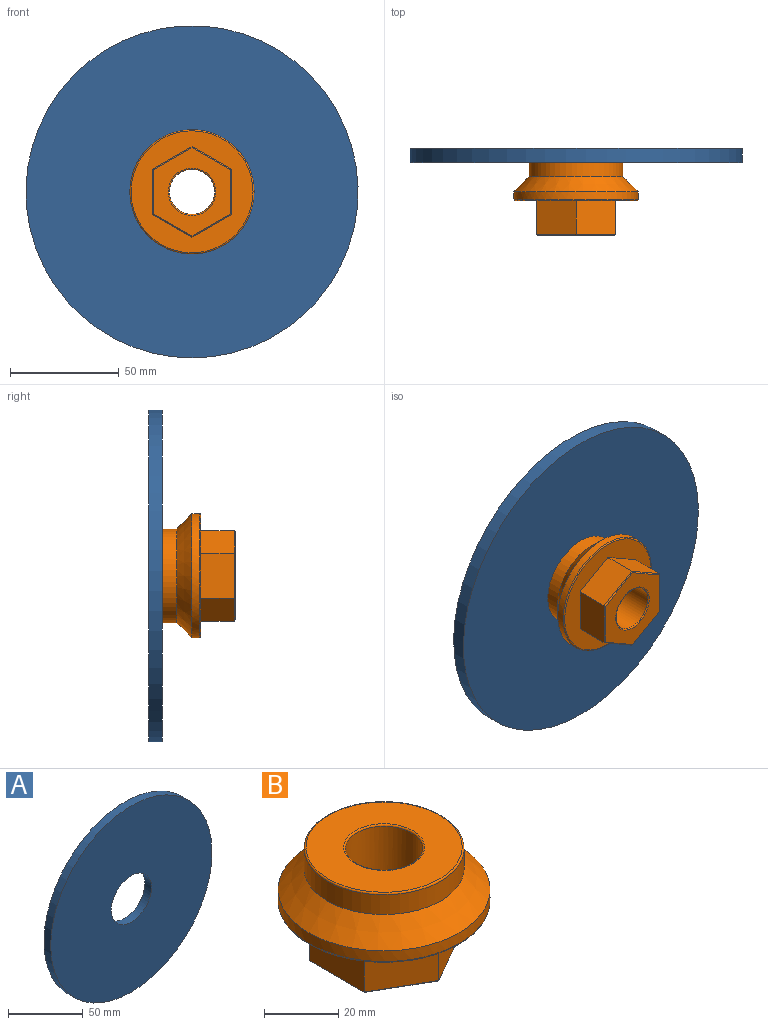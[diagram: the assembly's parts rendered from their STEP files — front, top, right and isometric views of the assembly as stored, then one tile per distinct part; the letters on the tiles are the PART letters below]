
ASSEMBLY  parts=2 mates=1
PART A: 4 faces, bbox 152.4x6.4x152.4 mm
  f0: cylinder r=19.05mm len=38.1mm, axis (0,1,0), area 760.1mm2, adj f2,f3
  f1: cylinder r=76.2mm len=152.4mm, axis (0,1,0), area 3040.2mm2, adj f2,f3
  f2: plane 152.4x152.4mm, normal (0,-1,0), area 17101.4mm2, adj f0,f1
  f3: plane 152.4x152.4mm, normal (0,1,0), area 17101.4mm2, adj f0,f1
PART B: 23 faces, bbox 61.7x61.7x34 mm
  f0: plane 18x10.68mm, normal (-0.35,-0.61,-0.71), area 14.5mm2, adj f4,f5,f9,f21
  f1: plane 18x10.68mm, normal (-0.35,0.61,-0.71), area 14.5mm2, adj f2,f5,f8,f9
  f2: plane 18x10.68mm, normal (0.35,0.61,-0.71), area 14.5mm2, adj f1,f3,f7,f9
  f3: plane 20.78x0.5mm, normal (0.71,0,-0.71), area 14.5mm2, adj f2,f4,f6,f9
  f4: plane 18x10.68mm, normal (0.35,-0.61,-0.71), area 14.5mm2, adj f0,f3,f9,f20
  f5: plane 20.78x0.5mm, normal (-0.71,0,-0.71), area 14.5mm2, adj f0,f1,f9,f22
  f6: plane 20.78x15.5mm, normal (1,0,0), area 322.2mm2, adj f3,f7,f14,f20
  f7: plane 18x15.5mm, normal (0.5,0.87,0), area 322.2mm2, adj f2,f6,f8,f14
  f8: plane 18x15.5mm, normal (-0.5,0.87,0), area 322.2mm2, adj f1,f7,f14,f22
  f9: plane 40.41x35mm, normal (0,0,-1), area 689.3mm2, adj f0,f1,f2,f3,f4,f5,f10
  f10: torus R=10.88mm, axis (0,0,1), area 52.1mm2, adj f9,f11
  f11: cylinder r=10.38mm len=33mm, axis (0,0,-1), area 2151.4mm2, adj f10,f15
  f12: torus R=28mm, axis (0,0,1), area 139.7mm2, adj f13,f14
  f13: cylinder r=28.5mm len=57mm, axis (0,0,1), area 626.7mm2, adj f12,f19
  f14: plane 56x56mm, normal (0,0,-1), area 1340.6mm2, adj f6,f7,f8,f12,f20,f21,f22
  f15: torus R=10.88mm, axis (0,0,-1), area 52.1mm2, adj f11,f16
  f16: plane 42x42mm, normal (0,0,1), area 1013.8mm2, adj f15,f17
  f17: torus R=21mm, axis (0,0,1), area 105.2mm2, adj f16,f18
  f18: cylinder r=21.5mm len=43mm, axis (0,0,-1), area 878.1mm2, adj f17,f19
  f19: cone r=25mm half-angle=45deg, axis (0,0,-1), area 1555mm2, adj f13,f18
  f20: plane 18x15.5mm, normal (0.5,-0.87,0), area 322.2mm2, adj f4,f6,f14,f21
  f21: plane 18x15.5mm, normal (-0.5,-0.87,0), area 322.2mm2, adj f0,f14,f20,f22
  f22: plane 20.78x15.5mm, normal (-1,0,0), area 322.2mm2, adj f5,f8,f14,f21
PLACE A t=(4.81,4.55,2.67)mm fixed
PLACE B rot(axis=(-1,0,0),90deg) t=(4.81,-32.12,2.67)mm
MATE cylindrical B.f10 <-> A.f0  axis (0,-1,0) through (4.81,1.38,2.67)mm
